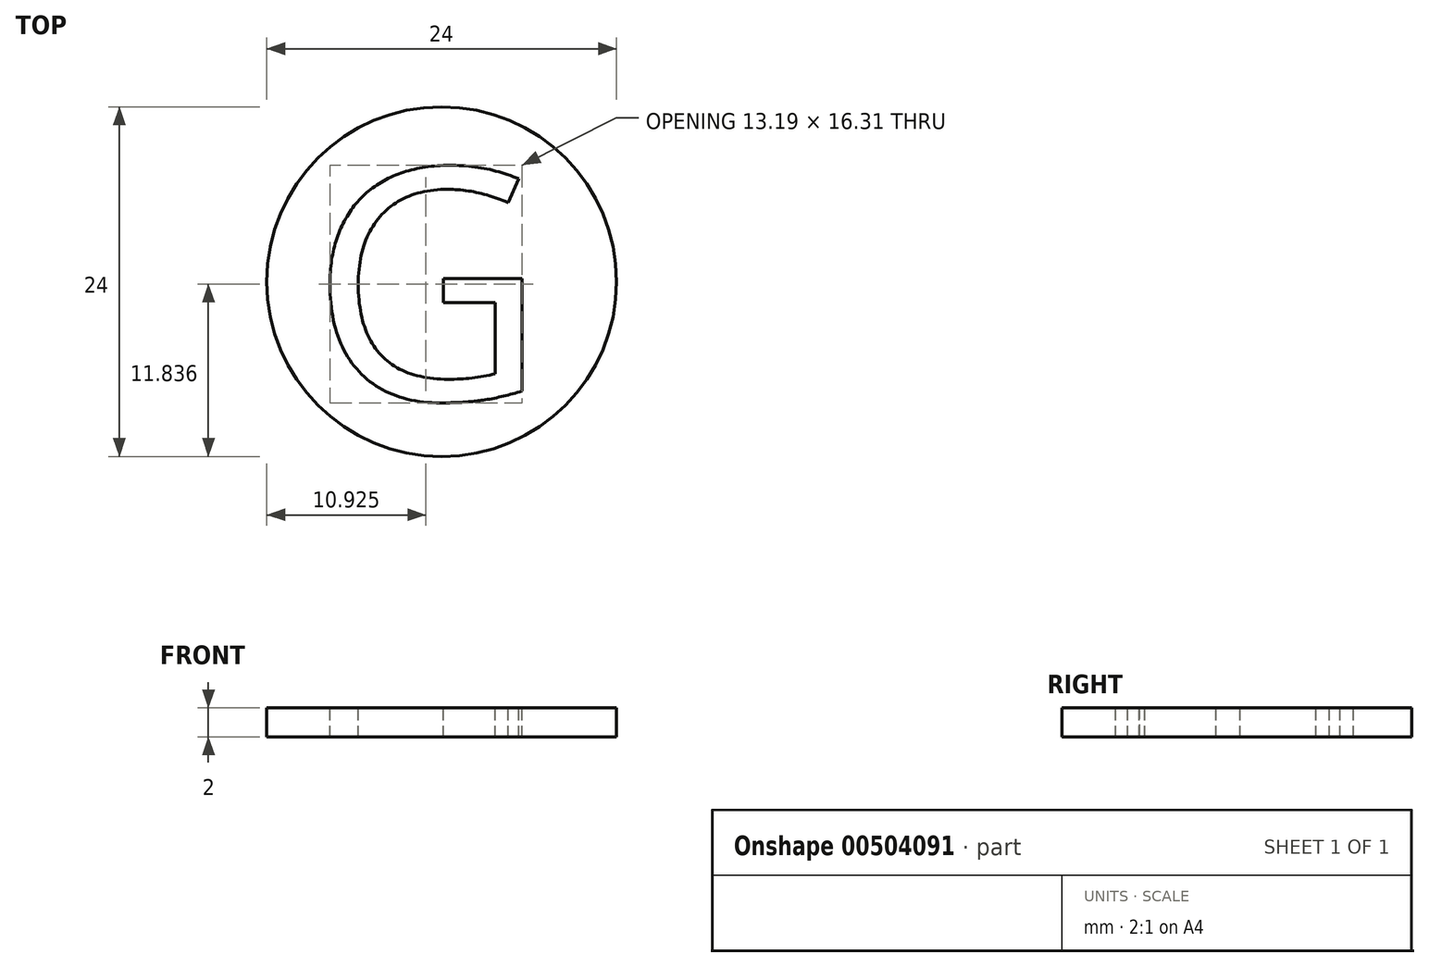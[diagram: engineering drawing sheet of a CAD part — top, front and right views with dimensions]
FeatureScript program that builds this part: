
annotation { "Feature Type Name" : "Feature", "Feature Type Description" : "" }
export const myFeature = defineFeature(function(context is Context, id is Id, definition is map)
    precondition{}
    {
        {
            var Q0;
            Q0=qCreatedBy(makeId("Top.planeOp"),FACE);
            var sketch = newSketch(context, id + "F0", { "sketchPlane" : qUnion([Q0])});
            skCircle(sketch, "E0", {"center": v(0, 0) * mm, "radius": 12 * mm});
            skSolve(sketch);
        }
        {
            var Q0;
            Q0=qSketchRegion(id+"F0",true);
            extrude(context, id + "F1", {"entities" : qUnion([Q0]), "depth" : 2 * mm});
        }
        {
            var Q0;
            Q0=makeQuery(id+"F1.opExtrude","CAP_FACE",FACE,{"disambiguationData":[OSD([sQuery(id+"F0.wireOp",EDGE,"E0")])],"isStart":false});
            var sketch = newSketch(context, id + "F2", { "sketchPlane" : qUnion([Q0])});
            skPoint(sketch, "E1", {"position": v(0, 12) * mm});
            skText(sketch, "E2", { "text": "G", "fontName": "OpenSans-Regular.ttf"});
            const initialGuessF2  = {"E2": [-0.00903, -0.0081, 1, 0, 0.016]};
            skSetInitialGuess(sketch, initialGuessF2);
            skSolve(sketch);
        }
        {
            var Q0;
            Q0=qSketchRegion(id+"F2",true);
            extrude(context, id + "F3", {"entities" : qUnion([Q0]), "operationType" : NewBodyOperationType.REMOVE, "oppositeDirection" : true, "depth" : 25 * mm});
        }
    });
